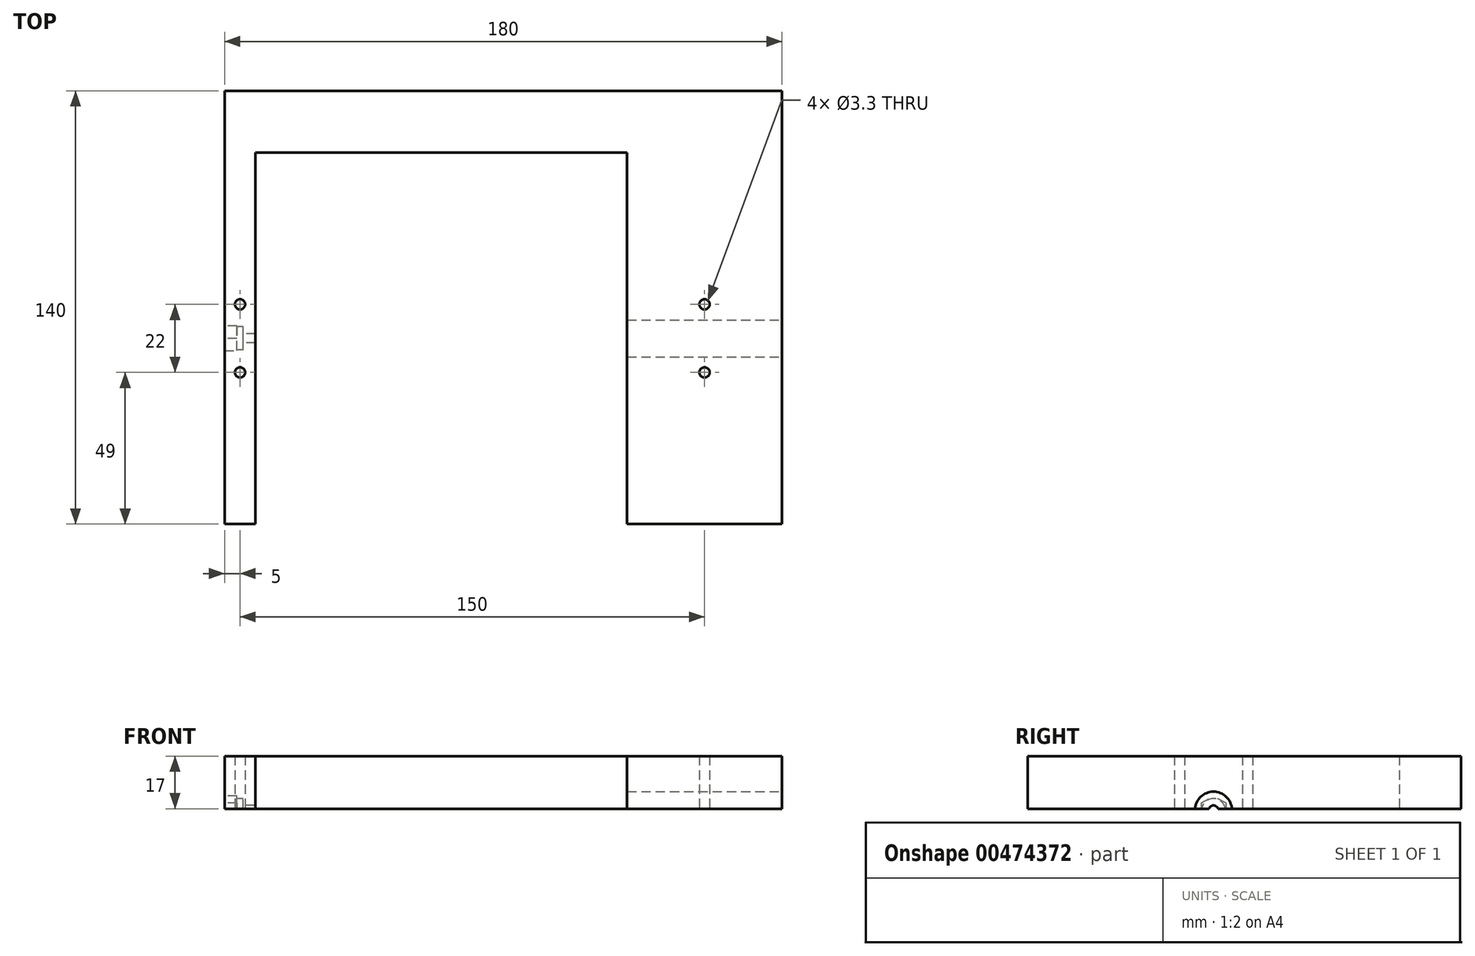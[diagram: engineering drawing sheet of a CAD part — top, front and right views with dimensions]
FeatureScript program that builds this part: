
annotation { "Feature Type Name" : "Feature", "Feature Type Description" : "" }
export const myFeature = defineFeature(function(context is Context, id is Id, definition is map)
    precondition{}
    {
        {
            var Q0;
            Q0=qCreatedBy(makeId("Top.planeOp"),FACE);
            var sketch = newSketch(context, id + "F0", { "sketchPlane" : qUnion([Q0])});
            skLineSegment(sketch, "E0.bottom", {"start": v(-90, -70) * mm, "end": v(90, -70) * mm});
            skLineSegment(sketch, "E0.top", {"start": v(-90, 70) * mm, "end": v(90, 70) * mm});
            skLineSegment(sketch, "E0.left", {"start": v(-90, -70) * mm, "end": v(-90, 70) * mm});
            skLineSegment(sketch, "E0.right", {"start": v(90, -70) * mm, "end": v(90, 70) * mm});
            skPoint(sketch, "E0.middle", {"position": v(0, 0) * mm});
            skSolve(sketch);
        }
        {
            var Q0;
            Q0=qSketchRegion(id+"F0",true);
            extrude(context, id + "F1", {"entities" : qUnion([Q0]), "depth" : 30 * mm});
        }
        {
            var Q0;
            Q0=makeQuery(id+"F1.opExtrude","SWEPT_FACE",FACE,{"disambiguationData":[OSD([sQuery(id+"F0.wireOp",EDGE,"E0.left")])]});
            var sketch = newSketch(context, id + "F2", { "sketchPlane" : qUnion([Q0])});
            skPoint(sketch, "E1.endSnap0", {"position": v(0, 0) * mm});
            skLineSegment(sketch, "E2", {"start": v(-70, 15) * mm, "end": v(-50, 15) * mm, "construction": true});
            skLineSegment(sketch, "E3", {"start": v(70, 0) * mm, "end": v(70, 12.5) * mm, "construction": true});
            skLineSegment(sketch, "E4", {"start": v(70, 12.5) * mm, "end": v(10, 12.5) * mm, "construction": true});
            skLineSegment(sketch, "E5", {"start": v(10, 12.5) * mm, "end": v(10, 17.12) * mm, "construction": true});
            skLineSegment(sketch, "E6", {"start": v(10, 12.5) * mm, "end": v(14, 14.8) * mm, "construction": true});
            skLineSegment(sketch, "E7.MirrorCS", {"start": v(10, 12.5) * mm, "end": v(14, 10.2) * mm, "construction": true});
            skLineSegment(sketch, "E8.MirrorCS", {"start": v(10, 12.5) * mm, "end": v(10, 7.88) * mm, "construction": true});
            skLineSegment(sketch, "E9.MirrorCS", {"start": v(10, 12.5) * mm, "end": v(6, 10.19) * mm, "construction": true});
            skLineSegment(sketch, "E10.MirrorCS", {"start": v(10, 12.5) * mm, "end": v(6, 14.8) * mm, "construction": true});
            skLineSegment(sketch, "E11", {"start": v(6, 14.8) * mm, "end": v(10, 17.12) * mm});
            skLineSegment(sketch, "E12", {"start": v(6, 14.8) * mm, "end": v(6, 10.19) * mm});
            skLineSegment(sketch, "E13", {"start": v(6, 10.19) * mm, "end": v(10, 7.88) * mm});
            skLineSegment(sketch, "E14", {"start": v(10, 7.88) * mm, "end": v(14, 10.2) * mm});
            skLineSegment(sketch, "E15", {"start": v(14, 14.8) * mm, "end": v(14, 10.2) * mm});
            skLineSegment(sketch, "E16", {"start": v(14, 14.8) * mm, "end": v(10, 17.12) * mm});
            skLineSegment(sketch, "E17", {"start": v(6, 14.8) * mm, "end": v(14, 14.8) * mm, "construction": true});
            skSolve(sketch);
        }
        {
            var Q0;
            Q0=qCreatedBy(makeId("Top.planeOp"),FACE);
            var sketch = newSketch(context, id + "F3", { "sketchPlane" : qUnion([Q0])});
            skLineSegment(sketch, "E18.bottom", {"start": v(90, -70) * mm, "end": v(-90, -70) * mm, "construction": true});
            skLineSegment(sketch, "E18.top", {"start": v(90, 70) * mm, "end": v(-90, 70) * mm, "construction": true});
            skLineSegment(sketch, "E18.left", {"start": v(90, -70) * mm, "end": v(90, 70) * mm, "construction": true});
            skLineSegment(sketch, "E18.right", {"start": v(-90, -70) * mm, "end": v(-90, 70) * mm, "construction": true});
            skPoint(sketch, "E18.middle", {"position": v(0, 0) * mm});
            skLineSegment(sketch, "E19", {"start": v(90, -70) * mm, "end": v(40, -70) * mm, "construction": true});
            skLineSegment(sketch, "E20", {"start": v(40, -70) * mm, "end": v(40, 50) * mm});
            skLineSegment(sketch, "E21", {"start": v(40, 50) * mm, "end": v(-80, 50) * mm});
            skLineSegment(sketch, "E22", {"start": v(-80, 50) * mm, "end": v(-80, -70) * mm});
            skLineSegment(sketch, "E23", {"start": v(-90, -70) * mm, "end": v(-80, -70) * mm, "construction": true});
            skLineSegment(sketch, "E24", {"start": v(-80, -70) * mm, "end": v(40, -70) * mm});
            skSolve(sketch);
        }
        {
            var Q0;
            Q0=qSketchRegion(id+"F3",true);
            var Q1;
            Q1=makeQuery(id+"F1.opExtrude","CAP_FACE",FACE,{"disambiguationData":[OSD([sQuery(id+"F0.wireOp",EDGE,"E0.bottom"),sQuery(id+"F0.wireOp",EDGE,"E0.top"),sQuery(id+"F0.wireOp",EDGE,"E0.left"),sQuery(id+"F0.wireOp",EDGE,"E0.right")])],"isStart":false});
            extrude(context, id + "F4", {"entities" : qUnion([Q0]), "operationType" : NewBodyOperationType.REMOVE, "endBound" : BoundingType.UP_TO_SURFACE, "endBoundEntityFace" : qUnion([Q1]), "depth" : 25 * mm});
        }
        {
            var Q0;
            Q0=qSketchRegion(id+"F2",true);
            extrude(context, id + "F5", {"entities" : qUnion([Q0]), "operationType" : NewBodyOperationType.REMOVE, "oppositeDirection" : true, "depth" : 4 * mm});
        }
        {
            var Q0;
            Q0=makeQuery(id+"F5.boolean.opBoolean","COPY",FACE,{"derivedFrom":makeQuery(id+"F5.opExtrude","CAP_FACE",FACE,{"disambiguationData":[OSD([sQuery(id+"F2.wireOp",EDGE,"E11"),sQuery(id+"F2.wireOp",EDGE,"E12"),sQuery(id+"F2.wireOp",EDGE,"E13"),sQuery(id+"F2.wireOp",EDGE,"E14"),sQuery(id+"F2.wireOp",EDGE,"E15"),sQuery(id+"F2.wireOp",EDGE,"E16")])],"isStart":false})});
            var sketch = newSketch(context, id + "F6", { "sketchPlane" : qUnion([Q0])});
            skCircle(sketch, "E25", {"center": v(10, 12.5) * mm, "radius": 3.8 * mm});
            skLineSegment(sketch, "E26", {"start": v(10, 17.12) * mm, "end": v(10, 7.88) * mm, "construction": true});
            skLineSegment(sketch, "E27", {"start": v(6, 10.19) * mm, "end": v(14, 14.8) * mm, "construction": true});
            skSolve(sketch);
        }
        {
            var Q0;
            Q0=qSketchRegion(id+"F6",true);
            extrude(context, id + "F7", {"entities" : qUnion([Q0]), "operationType" : NewBodyOperationType.REMOVE, "oppositeDirection" : true, "depth" : 2 * mm});
        }
        {
            var Q0;
            Q0=makeQuery(id+"F7.boolean.opBoolean","COPY",FACE,{"derivedFrom":makeQuery(id+"F7.opExtrude","CAP_FACE",FACE,{"disambiguationData":[OSD([sQuery(id+"F6.wireOp",EDGE,"E25")])],"isStart":false})});
            var sketch = newSketch(context, id + "F8", { "sketchPlane" : qUnion([Q0])});
            skCircle(sketch, "E28", {"center": v(10, 12.5) * mm, "radius": 1.55 * mm});
            skSolve(sketch);
        }
        {
            var Q0;
            Q0=qSketchRegion(id+"F8",true);
            extrude(context, id + "F9", {"entities" : qUnion([Q0]), "operationType" : NewBodyOperationType.REMOVE, "oppositeDirection" : true, "depth" : 7 * mm});
        }
        {
            var Q0;
            Q0=makeQuery(id+"F1.opExtrude","SWEPT_FACE",FACE,{"disambiguationData":[OSD([sQuery(id+"F0.wireOp",EDGE,"E0.right")])]});
            var sketch = newSketch(context, id + "F10", { "sketchPlane" : qUnion([Q0])});
            skLineSegment(sketch, "E29", {"start": v(-70, 0) * mm, "end": v(-70, 12.5) * mm, "construction": true});
            skLineSegment(sketch, "E30", {"start": v(-70, 12.5) * mm, "end": v(-10, 12.5) * mm, "construction": true});
            skCircle(sketch, "E31", {"center": v(-10, 12.5) * mm, "radius": 6 * mm});
            skSolve(sketch);
        }
        {
            var Q0;
            Q0=makeQuery(id+"F1.opExtrude","SWEPT_FACE",FACE,{"disambiguationData":[OSD([sQuery(id+"F0.wireOp",EDGE,"E0.top")])]});
            var sketch = newSketch(context, id + "F11", { "sketchPlane" : qUnion([Q0])});
            skPoint(sketch, "E32.endSnap0", {"position": v(0, 0) * mm});
            skLineSegment(sketch, "E33", {"start": v(-90, 6) * mm, "end": v(-65, 6) * mm, "construction": true});
            skPoint(sketch, "E34", {"position": v(-65, 6) * mm});
            skLineSegment(sketch, "E35", {"start": v(90, 6) * mm, "end": v(80, 6) * mm, "construction": true});
            skLineSegment(sketch, "E36", {"start": v(-5, 6) * mm, "end": v(20, 6) * mm, "construction": true});
            skCircle(sketch, "E37", {"center": v(20, 6) * mm, "radius": 0.5 * mm});
            skLineSegment(sketch, "E38", {"start": v(20, 6) * mm, "end": v(80, 6) * mm, "construction": true});
            skLineSegment(sketch, "E39", {"start": v(0, 0) * mm, "end": v(-5, 0) * mm, "construction": true});
            skLineSegment(sketch, "E40", {"start": v(0, 0) * mm, "end": v(0, 6) * mm, "construction": true});
            skCircle(sketch, "E41", {"center": v(-5, 6) * mm, "radius": 0.5 * mm});
            skLineSegment(sketch, "E42", {"start": v(-65, 6) * mm, "end": v(-5, 6) * mm, "construction": true});
            skSolve(sketch);
        }
        {
            var Q0;
            Q0=makeQuery(id+"F10.imprint","IMPRINT",FACE,{"disambiguationData":[TD([[makeQuery(id+"F10.imprint","IMPRINT",EDGE,{"derivedFrom":sQuery(id+"F10.wireOp",EDGE,"E31")}),1.0]])]});
            var Q1;
            Q1=makeQuery(id+"F4.boolean.opBoolean","COPY",FACE,{"derivedFrom":makeQuery(id+"F4.opExtrude","SWEPT_FACE",FACE,{"disambiguationData":[OSD([sQuery(id+"F3.wireOp",EDGE,"E20")])]})});
            extrude(context, id + "F12", {"entities" : qUnion([Q0]), "operationType" : NewBodyOperationType.REMOVE, "endBound" : BoundingType.UP_TO_SURFACE, "oppositeDirection" : true, "endBoundEntityFace" : qUnion([Q1]), "depth" : 25 * mm});
        }
        {
            var Q0;
            Q0=qSketchRegion(id+"F11",true);
            var Q1;
            Q1=makeQuery(id+"F4.boolean.opBoolean","COPY",FACE,{"derivedFrom":makeQuery(id+"F4.opExtrude","SWEPT_FACE",FACE,{"disambiguationData":[OSD([sQuery(id+"F3.wireOp",EDGE,"YkLpMczh-LnJE-8Oms-Y8Ta-dxZD4QefJqg7")])]})});
            extrude(context, id + "F13", {"entities" : qUnion([Q0]), "operationType" : NewBodyOperationType.REMOVE, "oppositeDirection" : true, "endBoundEntityFace" : qUnion([Q1]), "depth" : 1 * mm});
        }
        {
            var Q0;
            Q0=qCreatedBy(makeId("Top.planeOp"),FACE);
            var sketch = newSketch(context, id + "F14", { "sketchPlane" : qUnion([Q0])});
            skLineSegment(sketch, "E43.bottom", {"start": v(90, 70) * mm, "end": v(-90, 70) * mm});
            skLineSegment(sketch, "E43.top", {"start": v(90, -70) * mm, "end": v(-90, -70) * mm});
            skLineSegment(sketch, "E43.left", {"start": v(90, 70) * mm, "end": v(90, -70) * mm});
            skLineSegment(sketch, "E43.right", {"start": v(-90, 70) * mm, "end": v(-90, -70) * mm});
            skPoint(sketch, "E43.middle", {"position": v(0, 0) * mm});
            skSolve(sketch);
        }
        {
            var Q0;
            Q0=qSketchRegion(id+"F14",true);
            extrude(context, id + "F15", {"entities" : qUnion([Q0]), "operationType" : NewBodyOperationType.REMOVE, "depth" : 13 * mm});
        }
        {
            var Q0;
            Q0=qCreatedBy(makeId("Top.planeOp"),FACE);
            var sketch = newSketch(context, id + "F16", { "sketchPlane" : qUnion([Q0])});
            skPoint(sketch, "E44.middle", {"position": v(0, 0) * mm});
            skLineSegment(sketch, "E45.bottom", {"start": v(-90, -70) * mm, "end": v(90, -70) * mm, "construction": true});
            skLineSegment(sketch, "E45.top", {"start": v(-90, 70) * mm, "end": v(90, 70) * mm, "construction": true});
            skLineSegment(sketch, "E45.left", {"start": v(-90, -70) * mm, "end": v(-90, 70) * mm, "construction": true});
            skLineSegment(sketch, "E45.right", {"start": v(90, -70) * mm, "end": v(90, 70) * mm, "construction": true});
            skLineSegment(sketch, "E46", {"start": v(-90, -70) * mm, "end": v(-85, -70) * mm, "construction": true});
            skLineSegment(sketch, "E47", {"start": v(-85, -70) * mm, "end": v(-85, -10) * mm, "construction": true});
            skLineSegment(sketch, "E48", {"start": v(-85, -10) * mm, "end": v(65, -10) * mm, "construction": true});
            skLineSegment(sketch, "E49", {"start": v(65, -10) * mm, "end": v(65, -70) * mm, "construction": true});
            skLineSegment(sketch, "E50", {"start": v(-85, -10) * mm, "end": v(-85, -21) * mm, "construction": true});
            skLineSegment(sketch, "E51", {"start": v(-85, -10) * mm, "end": v(-85, 1) * mm, "construction": true});
            skCircle(sketch, "E52", {"center": v(-85, 1) * mm, "radius": 1.65 * mm});
            skCircle(sketch, "E53", {"center": v(-85, -21) * mm, "radius": 1.65 * mm});
            skLineSegment(sketch, "E54", {"start": v(65, -10) * mm, "end": v(65, 1) * mm, "construction": true});
            skLineSegment(sketch, "E55", {"start": v(65, -10) * mm, "end": v(65, -21) * mm, "construction": true});
            skCircle(sketch, "E56", {"center": v(65, 1) * mm, "radius": 1.65 * mm});
            skCircle(sketch, "E57", {"center": v(65, -21) * mm, "radius": 1.65 * mm});
            skSolve(sketch);
        }
        {
            var Q0;
            Q0=qSketchRegion(id+"F16",true);
            var Q1;
            Q1=makeQuery(id+"F1.opExtrude","CAP_FACE",FACE,{"disambiguationData":[OSD([sQuery(id+"F0.wireOp",EDGE,"E0.bottom"),sQuery(id+"F0.wireOp",EDGE,"E0.top"),sQuery(id+"F0.wireOp",EDGE,"E0.left"),sQuery(id+"F0.wireOp",EDGE,"E0.right")])],"isStart":false});
            extrude(context, id + "F17", {"entities" : qUnion([Q0]), "operationType" : NewBodyOperationType.REMOVE, "endBound" : BoundingType.UP_TO_SURFACE, "endBoundEntityFace" : qUnion([Q1]), "depth" : 25 * mm});
        }
    });
